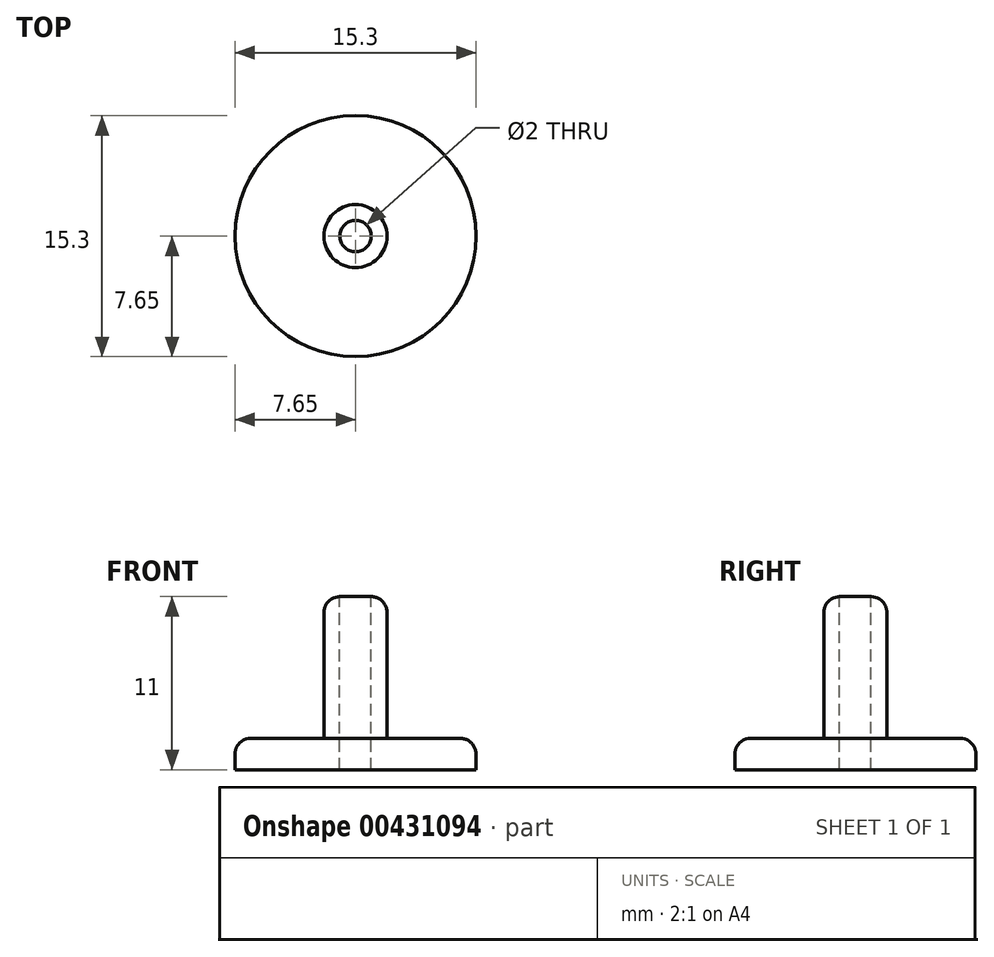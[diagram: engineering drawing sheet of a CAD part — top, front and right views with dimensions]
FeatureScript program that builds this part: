
annotation { "Feature Type Name" : "Feature", "Feature Type Description" : "" }
export const myFeature = defineFeature(function(context is Context, id is Id, definition is map)
    precondition{}
    {
        {
            var Q0;
            Q0=qCreatedBy(makeId("Top.planeOp"),FACE);
            var sketch = newSketch(context, id + "F0", { "sketchPlane" : qUnion([Q0])});
            skLineSegment(sketch, "E0", {"start": v(7.75, 0) * mm, "end": v(-7.75, 0) * mm, "construction": true});
            skLineSegment(sketch, "E1", {"start": v(0, -7.75) * mm, "end": v(0, 7.75) * mm, "construction": true});
            skCircle(sketch, "E2", {"center": v(0, 0) * mm, "radius": 7.65 * mm});
            skCircle(sketch, "E3", {"center": v(0, 0) * mm, "radius": 1 * mm});
            skSolve(sketch);
        }
        {
            var Q0;
            Q0=makeQuery(id+"F0.imprint","IMPRINT",FACE,{"disambiguationData":[TD([[makeQuery(id+"F0.imprint","IMPRINT",EDGE,{"derivedFrom":sQuery(id+"F0.wireOp",EDGE,"E2")}),1.0]])]});
            var sketch = newSketch(context, id + "F1", { "sketchPlane" : qUnion([Q0])});
            skCircle(sketch, "E4", {"center": v(0, 0) * mm, "radius": 2 * mm});
            skCircle(sketch, "E5", {"center": v(0, 0) * mm, "radius": 1 * mm});
            skSolve(sketch);
        }
        {
            var Q0;
            Q0 = qSketchRegion(id + "F0", true);
            extrude(context, id + "F2", {"entities" : qUnion([Q0]), "oppositeDirection" : true, "depth" : 2 * mm});
        }
        {
            var Q0;
            Q0 = qSketchRegion(id + "F1", true);
            extrude(context, id + "F3", {"entities" : qUnion([Q0]), "operationType" : NewBodyOperationType.ADD, "depth" : 9 * mm});
        }
        {
            var Q0;
            Q0=makeQuery(id+"F3.opExtrude","CAP_EDGE",EDGE,{"disambiguationData":[OSD([sQuery(id+"F1.wireOp",EDGE,"E4")])],"isStart":false});
            fillet(context, id + "F4", {"entities" : qUnion([Q0]), "radius" : 1 * mm, "tangentPropagation" : true, "allowEdgeOverflow" : false});
        }
        {
            var Q0;
            Q0=makeQuery(id+"F2.opExtrude","CAP_EDGE",EDGE,{"disambiguationData":[OSD([sQuery(id+"F0.wireOp",EDGE,"E2")])],"isStart":true});
            fillet(context, id + "F5", {"entities" : qUnion([Q0]), "radius" : 1 * mm, "tangentPropagation" : true, "allowEdgeOverflow" : false});
        }
    });
